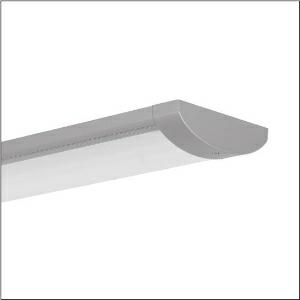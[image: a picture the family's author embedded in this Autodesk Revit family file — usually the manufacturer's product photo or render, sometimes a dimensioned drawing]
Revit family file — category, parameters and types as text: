
# Revit family: tv_20_5xa861d4n0j
name_source: partatom
category: Lighting Fixtures
units: mm (PartAtom-declared; Revit-internal decimal feet)

## family parameters
Cut with Voids When Loaded = No
Host = Face
Light Source = No
Part Type = Normal
Room Calculation Point = No
Round Connector Dimension = Use Diameter
Shared = No

## types (1)
- TV 20 (1 x LED 4000K / CRI = 80 (unbekannt), 3960 lm, 4000K)
    Apparent Load = 37 VA
    CIE Flux Codes = 48 78 95 99 100
    Color Rendering = 80
    Color Temperature = 4000K
    Default Elevation = 1800 mm
    Description = TV 20, vandal-proof luminaire, primary light control with specular reflector, of aluminium, matt, primary optical cover: enclosure, of PC, frosted, light emission: direct distribution, primary light characteristic: symmetric, installation type: surface-mounted, LED rated luminous flux: 3.960 lm, light colour: 840, colour temperature: 4000K, control gear: ECG DALI, mains connection: 230V, AC, 50Hz, rated input power: 37W, luminaire housing, of aluminium, coated, Siteco® metallic grey (DB 702S), length: 1.261 mm, width: 260 mm, height: 70mm, protection rating (complete): IP65, insulation class (complete): insulation class I (protective earthing), certification: CE, protection symbol: F, impact resistance: 2x IK10, standard: EN 60598, packaging unit: 1 piece
    Height = 70 mm
    Lamp = 1 x LED 4000K / CRI >= 80 (unbekannt)
    Lamp Light Flux = 3960 lm
    Lamp count = 1
    Length = 1261 mm
    Luminous efficacy = 107 lm/W
    Manufacturer = Siteco
    ModVariant = No
    Model = 5XA861D4N0J
    Mounting Place = Ceiling
    Mounting Type = Surface mounted
    Number of Poles = 1
    OnlyDefault = Yes
    Power Factor = 1
    Product Name = TV 20
    Product group = vandal-proof luminaire
    ProductGroupID = 307
    Protection Class = Protection class I
    Protection Degree = IP 65
    RLX_Detail_Level = 1
    RlxData = <blob elided: 25549 chars, md5=68f10264>
    Socket = socket
    Standby Power = 0 W
    System Light Flux = 3960 lm
    System Power = 37 W
    Type Comments = Product without accessories
    Type Image = l_1004809.jpg
    URL = http://relux.com
    VarID = ---
    Voltage = 0 V
    Weight = 0.00 kg
    Width = 260 mm

## geometry (parser evidence)
native form markers: Blend x4, Sweep x12
no freeform markers — native parametric forms only
